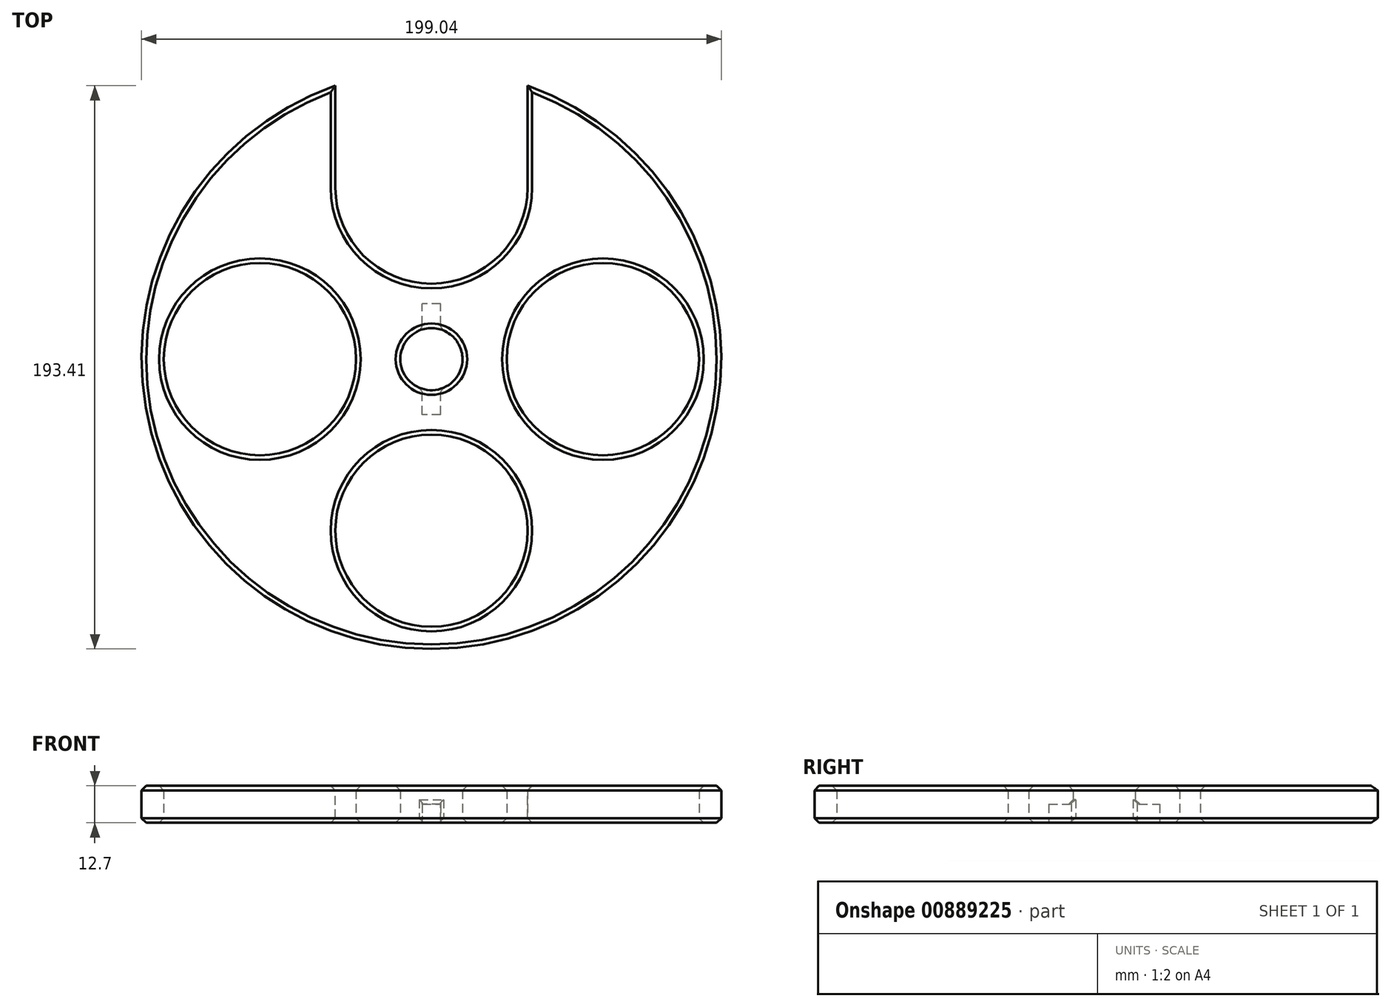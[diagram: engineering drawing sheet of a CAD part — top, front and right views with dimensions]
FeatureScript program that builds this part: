
annotation { "Feature Type Name" : "Feature", "Feature Type Description" : "" }
export const myFeature = defineFeature(function(context is Context, id is Id, definition is map)
    precondition{}
    {
        {
            var Q0;
            Q0=qCreatedBy(makeId("Top.planeOp"),FACE);
            var sketch = newSketch(context, id + "F0", { "sketchPlane" : qUnion([Q0])});
            skCircle(sketch, "E0", {"center": v(0, 0) * mm, "radius": 10.67 * mm});
            skCircle(sketch, "E1", {"center": v(0, 0) * mm, "radius": 7.9 * mm});
            skCircle(sketch, "E2", {"center": v(0, 0) * mm, "radius": 18.28 * mm, "construction": true});
            skCircle(sketch, "E3", {"center": v(0, 58.9) * mm, "radius": 40.62 * mm, "construction": true});
            skCircle(sketch, "E4", {"center": v(0, 58.9) * mm, "radius": 33 * mm});
            skCircle(sketch, "E5.1.0", {"center": v(-58.9, 0) * mm, "radius": 33 * mm});
            skCircle(sketch, "E5.2.0", {"center": v(0, -58.9) * mm, "radius": 33 * mm});
            skCircle(sketch, "E6.1.3.0", {"center": v(58.9, 0) * mm, "radius": 33 * mm});
            skCircle(sketch, "E7", {"center": v(58.9, 0) * mm, "radius": 40.62 * mm, "construction": true});
            skCircle(sketch, "E8", {"center": v(0, -58.9) * mm, "radius": 40.62 * mm, "construction": true});
            skCircle(sketch, "E9", {"center": v(-58.9, 0) * mm, "radius": 40.62 * mm, "construction": true});
            skCircle(sketch, "E10", {"center": v(0, 0) * mm, "radius": 109.54 * mm});
            skCircle(sketch, "E11", {"center": v(0, 0) * mm, "radius": 101.1 * mm});
            skLineSegment(sketch, "E12", {"start": v(0, 10.67) * mm, "end": v(0, 18.28) * mm, "construction": true});
            skLineSegment(sketch, "E13", {"start": v(0, 91.9) * mm, "end": v(0, 99.52) * mm, "construction": true});
            skCircle(sketch, "E14", {"center": v(0, 0) * mm, "radius": 99.52 * mm});
            skSolve(sketch);
        }
        {
            var Q0;
            Q0=makeQuery(id+"F0.imprint","IMPRINT",FACE,{"disambiguationData":[TD([[makeQuery(id+"F0.imprint","IMPRINT",EDGE,{"derivedFrom":sQuery(id+"F0.wireOp",EDGE,"E0")}),-1.0]])]});
            extrude(context, id + "F1", {"entities" : qUnion([Q0]), "depth" : 12.7 * mm, "offsetDistance" : 25.4 * mm});
        }
        {
            var Q0;
            Q0=makeQuery(id+"F1.opExtrude","CAP_FACE",FACE,{"disambiguationData":[OSD([sQuery(id+"F0.wireOp",EDGE,"E0"),sQuery(id+"F0.wireOp",EDGE,"E4"),sQuery(id+"F0.wireOp",EDGE,"E5.1.0"),sQuery(id+"F0.wireOp",EDGE,"E5.2.0"),sQuery(id+"F0.wireOp",EDGE,"E6.1.3.0"),sQuery(id+"F0.wireOp",EDGE,"E14")])],"isStart":true});
            var sketch = newSketch(context, id + "F2", { "sketchPlane" : qUnion([Q0])});
            skLineSegment(sketch, "E15.bottom", {"start": v(3.18, 19.05) * mm, "end": v(-3.17, 19.05) * mm});
            skLineSegment(sketch, "E15.top", {"start": v(3.18, -19.05) * mm, "end": v(-3.18, -19.05) * mm});
            skLineSegment(sketch, "E15.left", {"start": v(3.18, 19.05) * mm, "end": v(3.18, -19.05) * mm});
            skLineSegment(sketch, "E15.right", {"start": v(-3.17, 19.05) * mm, "end": v(-3.18, -19.05) * mm});
            skPoint(sketch, "E15.middle", {"position": v(0, 0) * mm});
            skSolve(sketch);
        }
        {
            var Q0;
            {var subQ0=sQuery(id+"F2.wireOp",EDGE,"E15.bottom");Q0=makeQuery(id+"F2.imprint","IMPRINT",FACE,{"disambiguationData":[TD([[makeQuery(id+"F2.imprint","IMPRINT",EDGE,{"derivedFrom":subQ0}),1.0]])]});}
            var Q1;
            {var subQ0=sQuery(id+"F2.wireOp",EDGE,"E15.top");Q1=makeQuery(id+"F2.imprint","IMPRINT",FACE,{"disambiguationData":[TD([[makeQuery(id+"F2.imprint","IMPRINT",EDGE,{"derivedFrom":subQ0}),-1.0]])]});}
            var Q2;
            {var subQ0=sQuery(id+"F2.wireOp",EDGE,"E15.left");var subQ1=sQuery(id+"F0.wireOp",EDGE,"E0");var subQ2=makeQuery(id+"F6.opChamfer","BLEND_EDGE",EDGE,{"blendedFrom":[makeQuery(id+"F1.opExtrude","CAP_EDGE",EDGE,{"disambiguationData":[OSD([subQ1])],"isStart":true}),makeQuery(id+"F1.opExtrude","CAP_FACE",FACE,{"disambiguationData":[OSD([subQ1,sQuery(id+"F0.wireOp",EDGE,"E4"),sQuery(id+"F0.wireOp",EDGE,"E5.1.0"),sQuery(id+"F0.wireOp",EDGE,"E5.2.0"),sQuery(id+"F0.wireOp",EDGE,"E6.1.3.0"),sQuery(id+"F0.wireOp",EDGE,"E14")])],"isStart":true})],"blendedInto":[makeQuery(id+"F1.opExtrude","CAP_FACE",FACE,{"disambiguationData":[OSD([subQ1,sQuery(id+"F0.wireOp",EDGE,"E4"),sQuery(id+"F0.wireOp",EDGE,"E5.1.0"),sQuery(id+"F0.wireOp",EDGE,"E5.2.0"),sQuery(id+"F0.wireOp",EDGE,"E6.1.3.0"),sQuery(id+"F0.wireOp",EDGE,"E14")])],"isStart":true})]});var subQ3=makeQuery(id+"F2.imprint","INTERSECT",VERTEX,{"disambiguationData":[OD(0.0)],"derivedFrom":[subQ2,subQ0]});Q2=makeQuery(id+"F2.imprint","IMPRINT",FACE,{"disambiguationData":[TD([[makeQuery(id+"F2.imprint","IMPRINT",EDGE,{"disambiguationData":[TD([[subQ3,-1.0]])],"derivedFrom":subQ0}),-1.0]])]});}
            extrude(context, id + "F3", {"entities" : qUnion([Q0, Q1, Q2]), "operationType" : NewBodyOperationType.REMOVE, "oppositeDirection" : true, "depth" : 6.35 * mm, "offsetDistance" : 25.4 * mm});
        }
        {
            var Q0;
            Q0=makeQuery(id+"F1.opExtrude","CAP_FACE",FACE,{"disambiguationData":[OSD([sQuery(id+"F0.wireOp",EDGE,"E0"),sQuery(id+"F0.wireOp",EDGE,"E4"),sQuery(id+"F0.wireOp",EDGE,"E5.1.0"),sQuery(id+"F0.wireOp",EDGE,"E5.2.0"),sQuery(id+"F0.wireOp",EDGE,"E6.1.3.0"),sQuery(id+"F0.wireOp",EDGE,"E14")])],"isStart":false});
            var sketch = newSketch(context, id + "F4", { "sketchPlane" : qUnion([Q0])});
            skLineSegment(sketch, "E16", {"start": v(-33, 58.9) * mm, "end": v(-33, 93.89) * mm});
            skLineSegment(sketch, "E17", {"start": v(33, 58.9) * mm, "end": v(33, 93.89) * mm});
            skArc(sketch, "E18", {"start": v(33, 93.89) * mm, "mid": v(0, 99.52) * mm, "end": v(-33, 93.89) * mm});
            skArc(sketch, "E19", {"start": v(33, 58.9) * mm, "mid": v(0, 91.9) * mm, "end": v(-33, 58.9) * mm});
            skSolve(sketch);
        }
        {
            var Q0;
            Q0=makeQuery(id+"F4.imprint","IMPRINT",FACE,{"disambiguationData":[TD([[makeQuery(id+"F4.imprint","IMPRINT",EDGE,{"derivedFrom":sQuery(id+"F4.wireOp",EDGE,"E16")}),-1.0]])]});
            extrude(context, id + "F5", {"entities" : qUnion([Q0]), "operationType" : NewBodyOperationType.REMOVE, "endBound" : BoundingType.THROUGH_ALL, "oppositeDirection" : true, "depth" : 25.4 * mm, "offsetDistance" : 25.4 * mm});
        }
        {
            var Q0;
            Q0=makeQuery(id+"F1.opExtrude","CAP_EDGE",EDGE,{"disambiguationData":[OSD([sQuery(id+"F0.wireOp",EDGE,"E0")])],"isStart":false});
            var Q1;
            Q1=makeQuery(id+"F1.opExtrude","CAP_EDGE",EDGE,{"disambiguationData":[OSD([sQuery(id+"F0.wireOp",EDGE,"E0")])],"isStart":true});
            var Q2;
            Q2=makeQuery(id+"F1.opExtrude","CAP_EDGE",EDGE,{"disambiguationData":[OSD([sQuery(id+"F0.wireOp",EDGE,"E14")])],"isStart":false});
            var Q3;
            Q3=makeQuery(id+"F1.opExtrude","CAP_EDGE",EDGE,{"disambiguationData":[OSD([sQuery(id+"F0.wireOp",EDGE,"E14")])],"isStart":true});
            var Q4;
            {var subQ1=sQuery(id+"F2.wireOp",EDGE,"E15.left");Q4=makeQuery(id+"F3.boolean.opBoolean","COPY",EDGE,{"disambiguationData":[TD([makeQuery(id+"F3.opExtrude","SWEPT_FACE",FACE,{"disambiguationData":[OSD([sQuery(id+"F2.wireOp",EDGE,"E15.bottom")])]})])],"derivedFrom":makeQuery(id+"F3.opExtrude","CAP_EDGE",EDGE,{"disambiguationData":[OSD([subQ1])],"isStart":true})});}
            var Q5;
            Q5=makeQuery(id+"F3.boolean.opBoolean","COPY",EDGE,{"derivedFrom":makeQuery(id+"F3.opExtrude","CAP_EDGE",EDGE,{"disambiguationData":[OSD([sQuery(id+"F2.wireOp",EDGE,"E15.bottom")])],"isStart":true})});
            var Q6;
            {var subQ1=sQuery(id+"F2.wireOp",EDGE,"E15.right");Q6=makeQuery(id+"F3.boolean.opBoolean","COPY",EDGE,{"disambiguationData":[TD([makeQuery(id+"F3.opExtrude","SWEPT_FACE",FACE,{"disambiguationData":[OSD([sQuery(id+"F2.wireOp",EDGE,"E15.bottom")])]})])],"derivedFrom":makeQuery(id+"F3.opExtrude","CAP_EDGE",EDGE,{"disambiguationData":[OSD([subQ1])],"isStart":true})});}
            var Q7;
            Q7=makeQuery(id+"F3.boolean.opBoolean","INTERSECT",EDGE,{"disambiguationData":[OD(0.0)],"derivedFrom":[makeQuery(id+"F1.opExtrude","SWEPT_FACE",FACE,{"disambiguationData":[OSD([sQuery(id+"F0.wireOp",EDGE,"E0")])]}),makeQuery(id+"F3.opExtrude","CAP_FACE",FACE,{"disambiguationData":[OSD([sQuery(id+"F2.wireOp",EDGE,"E15.bottom"),sQuery(id+"F2.wireOp",EDGE,"E15.top"),sQuery(id+"F2.wireOp",EDGE,"E15.left"),sQuery(id+"F2.wireOp",EDGE,"E15.right")])],"isStart":false})]});
            var Q8;
            Q8=makeQuery(id+"F3.boolean.opBoolean","INTERSECT",EDGE,{"disambiguationData":[OD(0.0)],"derivedFrom":[makeQuery(id+"F1.opExtrude","SWEPT_FACE",FACE,{"disambiguationData":[OSD([sQuery(id+"F0.wireOp",EDGE,"E0")])]}),makeQuery(id+"F3.opExtrude","SWEPT_FACE",FACE,{"disambiguationData":[OSD([sQuery(id+"F2.wireOp",EDGE,"E15.right")])]})]});
            var Q9;
            Q9=makeQuery(id+"F3.boolean.opBoolean","INTERSECT",EDGE,{"disambiguationData":[OD(0.0)],"derivedFrom":[makeQuery(id+"F1.opExtrude","SWEPT_FACE",FACE,{"disambiguationData":[OSD([sQuery(id+"F0.wireOp",EDGE,"E0")])]}),makeQuery(id+"F3.opExtrude","SWEPT_FACE",FACE,{"disambiguationData":[OSD([sQuery(id+"F2.wireOp",EDGE,"E15.left")])]})]});
            var Q10;
            Q10=makeQuery(id+"F3.boolean.opBoolean","INTERSECT",EDGE,{"disambiguationData":[OD(1.0)],"derivedFrom":[makeQuery(id+"F1.opExtrude","SWEPT_FACE",FACE,{"disambiguationData":[OSD([sQuery(id+"F0.wireOp",EDGE,"E0")])]}),makeQuery(id+"F3.opExtrude","SWEPT_FACE",FACE,{"disambiguationData":[OSD([sQuery(id+"F2.wireOp",EDGE,"E15.left")])]})]});
            var Q11;
            Q11=makeQuery(id+"F3.boolean.opBoolean","INTERSECT",EDGE,{"disambiguationData":[OD(1.0)],"derivedFrom":[makeQuery(id+"F1.opExtrude","SWEPT_FACE",FACE,{"disambiguationData":[OSD([sQuery(id+"F0.wireOp",EDGE,"E0")])]}),makeQuery(id+"F3.opExtrude","CAP_FACE",FACE,{"disambiguationData":[OSD([sQuery(id+"F2.wireOp",EDGE,"E15.bottom"),sQuery(id+"F2.wireOp",EDGE,"E15.top"),sQuery(id+"F2.wireOp",EDGE,"E15.left"),sQuery(id+"F2.wireOp",EDGE,"E15.right")])],"isStart":false})]});
            var Q12;
            Q12=makeQuery(id+"F3.boolean.opBoolean","INTERSECT",EDGE,{"disambiguationData":[OD(1.0)],"derivedFrom":[makeQuery(id+"F1.opExtrude","SWEPT_FACE",FACE,{"disambiguationData":[OSD([sQuery(id+"F0.wireOp",EDGE,"E0")])]}),makeQuery(id+"F3.opExtrude","SWEPT_FACE",FACE,{"disambiguationData":[OSD([sQuery(id+"F2.wireOp",EDGE,"E15.right")])]})]});
            var Q13;
            {var subQ1=sQuery(id+"F2.wireOp",EDGE,"E15.left");Q13=makeQuery(id+"F3.boolean.opBoolean","COPY",EDGE,{"disambiguationData":[TD([makeQuery(id+"F3.opExtrude","SWEPT_FACE",FACE,{"disambiguationData":[OSD([sQuery(id+"F2.wireOp",EDGE,"E15.top")])]})])],"derivedFrom":makeQuery(id+"F3.opExtrude","CAP_EDGE",EDGE,{"disambiguationData":[OSD([subQ1])],"isStart":true})});}
            var Q14;
            Q14=makeQuery(id+"F3.boolean.opBoolean","COPY",EDGE,{"derivedFrom":makeQuery(id+"F3.opExtrude","CAP_EDGE",EDGE,{"disambiguationData":[OSD([sQuery(id+"F2.wireOp",EDGE,"E15.top")])],"isStart":true})});
            var Q15;
            {var subQ1=sQuery(id+"F2.wireOp",EDGE,"E15.right");Q15=makeQuery(id+"F3.boolean.opBoolean","COPY",EDGE,{"disambiguationData":[TD([makeQuery(id+"F3.opExtrude","SWEPT_FACE",FACE,{"disambiguationData":[OSD([sQuery(id+"F2.wireOp",EDGE,"E15.top")])]})])],"derivedFrom":makeQuery(id+"F3.opExtrude","CAP_EDGE",EDGE,{"disambiguationData":[OSD([subQ1])],"isStart":true})});}
            var Q16;
            Q16=makeQuery(id+"F1.opExtrude","CAP_EDGE",EDGE,{"disambiguationData":[OSD([sQuery(id+"F0.wireOp",EDGE,"E6.1.3.0")])],"isStart":false});
            var Q17;
            Q17=makeQuery(id+"F1.opExtrude","CAP_EDGE",EDGE,{"disambiguationData":[OSD([sQuery(id+"F0.wireOp",EDGE,"E4")])],"isStart":false});
            var Q18;
            Q18=makeQuery(id+"F1.opExtrude","CAP_EDGE",EDGE,{"disambiguationData":[OSD([sQuery(id+"F0.wireOp",EDGE,"E5.2.0")])],"isStart":false});
            var Q19;
            Q19=makeQuery(id+"F1.opExtrude","CAP_EDGE",EDGE,{"disambiguationData":[OSD([sQuery(id+"F0.wireOp",EDGE,"E5.1.0")])],"isStart":false});
            var Q20;
            Q20=makeQuery(id+"F1.opExtrude","CAP_EDGE",EDGE,{"disambiguationData":[OSD([sQuery(id+"F0.wireOp",EDGE,"E5.1.0")])],"isStart":true});
            var Q21;
            Q21=makeQuery(id+"F1.opExtrude","CAP_EDGE",EDGE,{"disambiguationData":[OSD([sQuery(id+"F0.wireOp",EDGE,"E5.2.0")])],"isStart":true});
            var Q22;
            Q22=makeQuery(id+"F1.opExtrude","CAP_EDGE",EDGE,{"disambiguationData":[OSD([sQuery(id+"F0.wireOp",EDGE,"E4")])],"isStart":true});
            var Q23;
            Q23=makeQuery(id+"F1.opExtrude","CAP_EDGE",EDGE,{"disambiguationData":[OSD([sQuery(id+"F0.wireOp",EDGE,"E6.1.3.0")])],"isStart":true});
            chamfer(context, id + "F6", {"entities" : qUnion([Q0, Q1, Q2, Q3, Q4, Q5, Q6, Q7, Q8, Q9, Q10, Q11, Q12, Q13, Q14, Q15, Q16, Q17, Q18, Q19, Q20, Q21, Q22, Q23]), "width" : 1.59 * mm, "tangentPropagation" : true});
        }
    });
